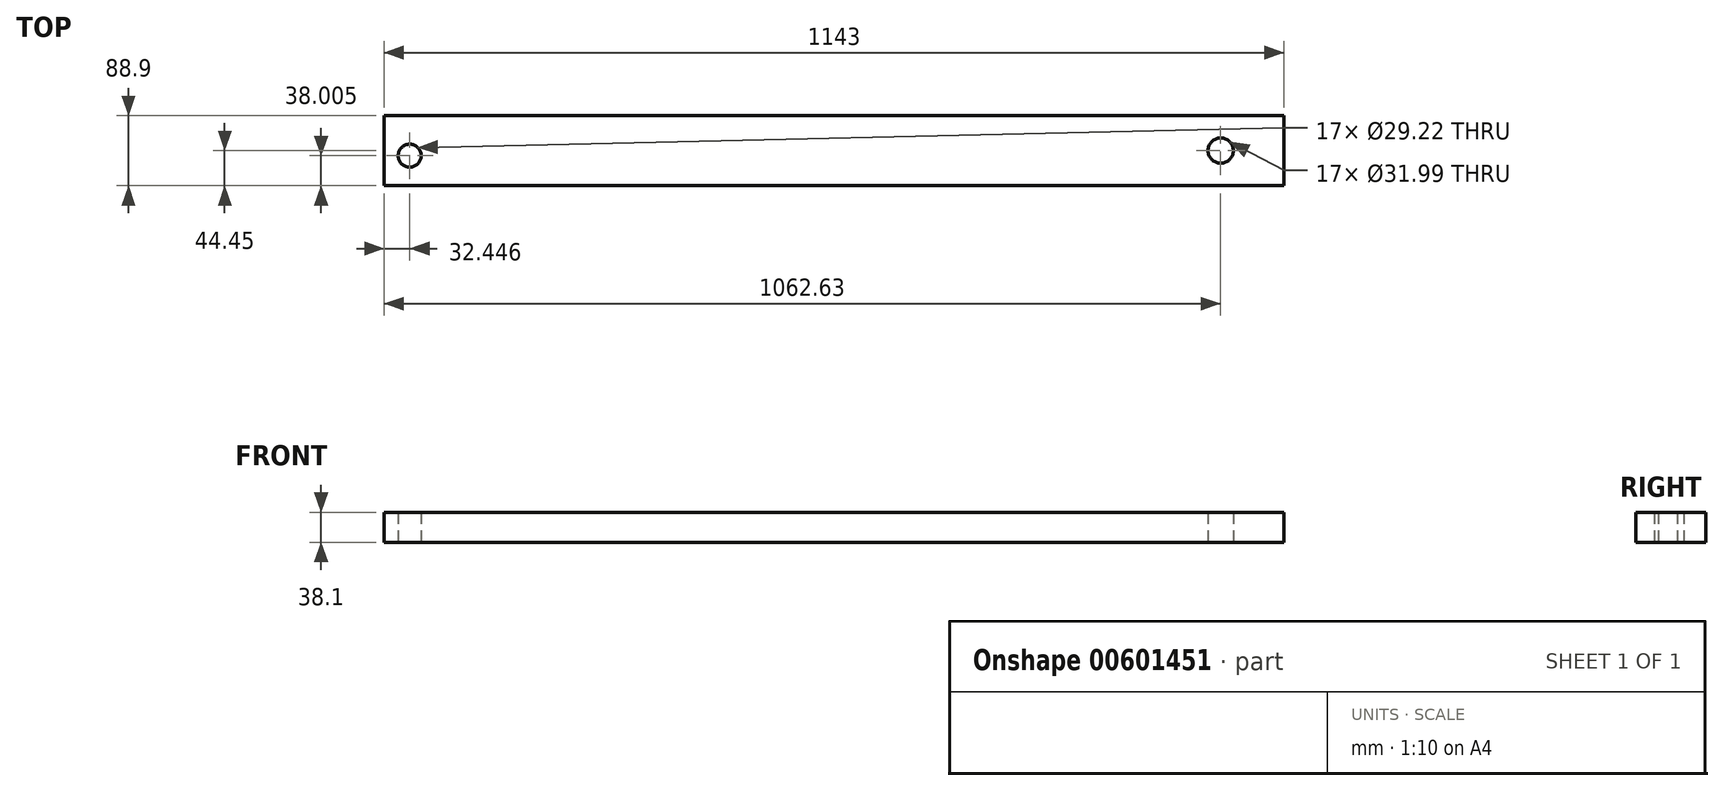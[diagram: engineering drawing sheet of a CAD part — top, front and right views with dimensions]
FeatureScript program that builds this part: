
annotation { "Feature Type Name" : "Feature", "Feature Type Description" : "" }
export const myFeature = defineFeature(function(context is Context, id is Id, definition is map)
    precondition{}
    {
        {
            var Q0;
            Q0=qCreatedBy(makeId("Top.planeOp"),FACE);
            var sketch = newSketch(context, id + "F0", { "sketchPlane" : qUnion([Q0])});
            skLineSegment(sketch, "E0.bottom", {"start": v(0, 0) * mm, "end": v(1143, 0) * mm});
            skLineSegment(sketch, "E0.top", {"start": v(0, 88.9) * mm, "end": v(1143, 88.9) * mm});
            skLineSegment(sketch, "E0.left", {"start": v(0, 0) * mm, "end": v(0, 88.9) * mm});
            skLineSegment(sketch, "E0.right", {"start": v(1143, 0) * mm, "end": v(1143, 88.9) * mm});
            skCircle(sketch, "E1", {"center": v(32.45, 38) * mm, "radius": 14.6 * mm});
            skCircle(sketch, "E2", {"center": v(1062.63, 44.45) * mm, "radius": 16 * mm});
            skPoint(sketch, "E2.centerSnap0", {"position": v(1143, 44.45) * mm});
            skSolve(sketch);
        }
        {
            var Q0;
            Q0=qSketchRegion(id+"F0",true);
            extrude(context, id + "F1", {"entities" : qUnion([Q0]), "depth" : 38.1 * mm, "offsetDistance" : 25.4 * mm});
        }
    });
